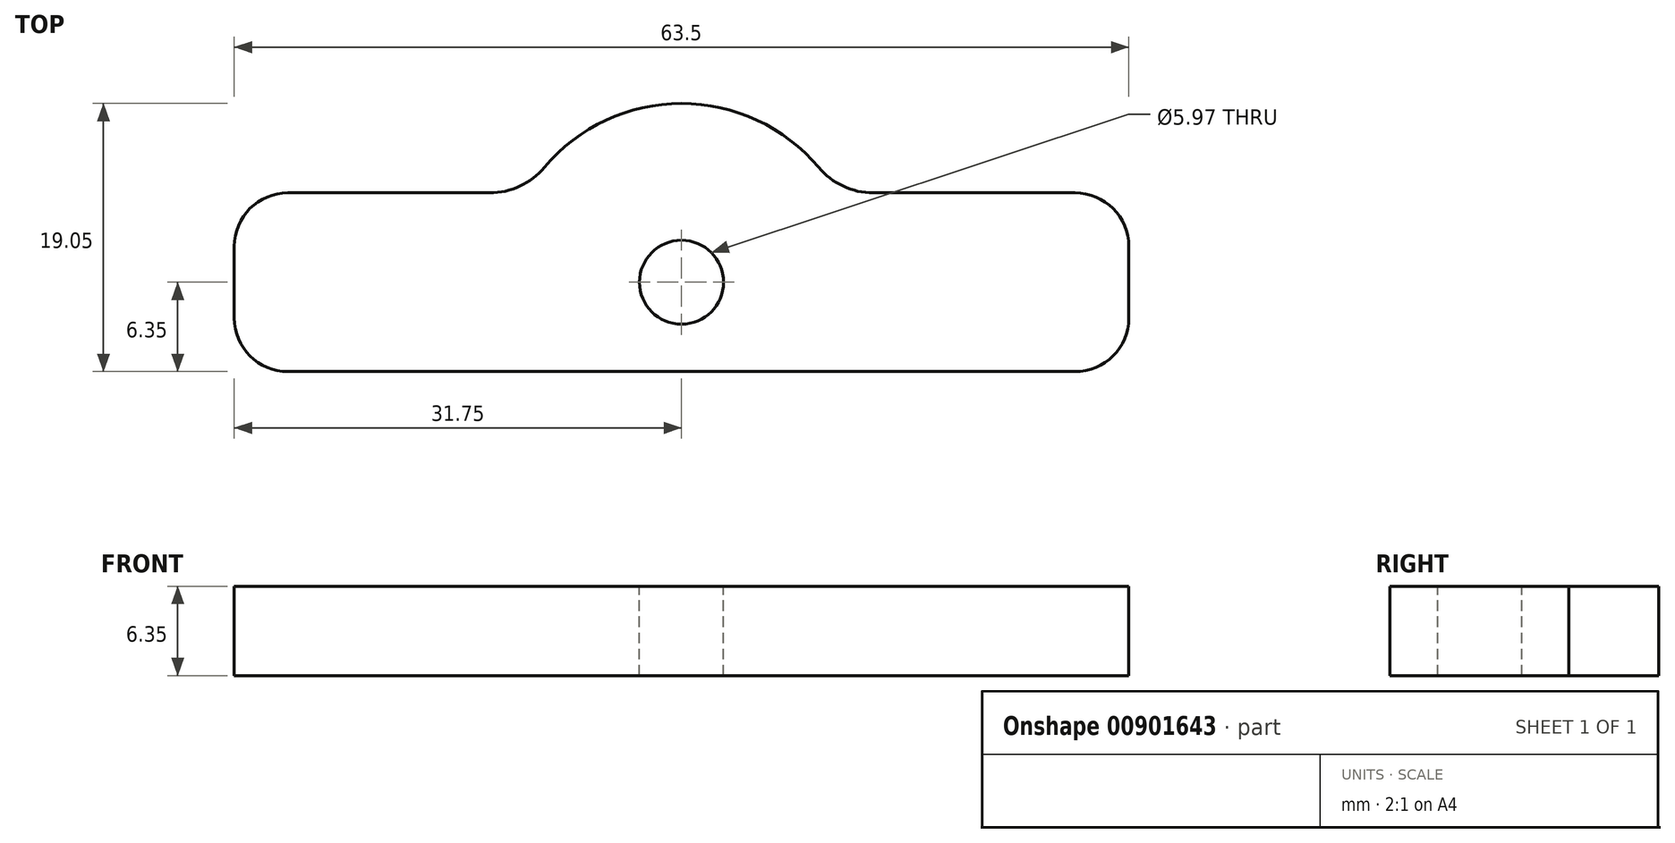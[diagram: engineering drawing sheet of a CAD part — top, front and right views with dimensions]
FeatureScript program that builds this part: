
annotation { "Feature Type Name" : "Feature", "Feature Type Description" : "" }
export const myFeature = defineFeature(function(context is Context, id is Id, definition is map)
    precondition{}
    {
        {
            var Q0;
            Q0=qCreatedBy(makeId("Top.planeOp"),FACE);
            var sketch = newSketch(context, id + "F0", { "sketchPlane" : qUnion([Q0])});
            skCircle(sketch, "E0", {"center": v(0, 0) * mm, "radius": 12.7 * mm});
            skLineSegment(sketch, "E1.bottom", {"start": v(31.75, 6.35) * mm, "end": v(-31.75, 6.35) * mm});
            skLineSegment(sketch, "E1.top", {"start": v(31.75, -6.35) * mm, "end": v(-31.75, -6.35) * mm});
            skLineSegment(sketch, "E1.left", {"start": v(31.75, 6.35) * mm, "end": v(31.75, -6.35) * mm});
            skLineSegment(sketch, "E1.right", {"start": v(-31.75, 6.35) * mm, "end": v(-31.75, -6.35) * mm});
            skSolve(sketch);
        }
        {
            var Q0;
            {var subQ0=sQuery(id+"F0.wireOp",EDGE,"E1.bottom");var subQ1=sQuery(id+"F0.wireOp",EDGE,"E0");var subQ2=makeQuery(id+"F0.imprint","INTERSECT",VERTEX,{"disambiguationData":[OD(0.0)],"derivedFrom":[subQ1,subQ0]});Q0=makeQuery(id+"F0.imprint","IMPRINT",FACE,{"disambiguationData":[TD([[makeQuery(id+"F0.imprint","IMPRINT",EDGE,{"disambiguationData":[TD([[subQ2,-1.0]])],"derivedFrom":subQ1}),1.0]])]});}
            var Q1;
            {var subQ5=sQuery(id+"F0.wireOp",EDGE,"E1.right");Q1=makeQuery(id+"F0.imprint","IMPRINT",FACE,{"disambiguationData":[TD([[makeQuery(id+"F0.imprint","IMPRINT",EDGE,{"derivedFrom":subQ5}),1.0]])]});}
            var Q2;
            {var subQ0=sQuery(id+"F0.wireOp",EDGE,"E1.bottom");var subQ1=sQuery(id+"F0.wireOp",EDGE,"E0");var subQ2=makeQuery(id+"F0.imprint","INTERSECT",VERTEX,{"disambiguationData":[OD(0.0)],"derivedFrom":[subQ1,subQ0]});Q2=makeQuery(id+"F0.imprint","IMPRINT",FACE,{"disambiguationData":[TD([[makeQuery(id+"F0.imprint","IMPRINT",EDGE,{"disambiguationData":[TD([[subQ2,1.0]])],"derivedFrom":subQ1}),1.0]])]});}
            var Q3;
            {var subQ5=sQuery(id+"F0.wireOp",EDGE,"E1.left");Q3=makeQuery(id+"F0.imprint","IMPRINT",FACE,{"disambiguationData":[TD([[makeQuery(id+"F0.imprint","IMPRINT",EDGE,{"derivedFrom":subQ5}),-1.0]])]});}
            var Q4;
            {var subQ0=sQuery(id+"F0.wireOp",EDGE,"E1.top");var subQ1=sQuery(id+"F0.wireOp",EDGE,"E0");var subQ2=makeQuery(id+"F0.imprint","INTERSECT",VERTEX,{"disambiguationData":[OD(0.0)],"derivedFrom":[subQ1,subQ0]});Q4=makeQuery(id+"F0.imprint","IMPRINT",FACE,{"disambiguationData":[TD([[makeQuery(id+"F0.imprint","IMPRINT",EDGE,{"disambiguationData":[TD([[subQ2,-1.0]])],"derivedFrom":subQ1}),1.0]])]});}
            extrude(context, id + "F1", {"entities" : qUnion([Q0, Q1, Q2, Q3, Q4]), "depth" : 6.35 * mm, "offsetDistance" : 25.4 * mm});
        }
        {
            var Q0;
            Q0=makeQuery(id+"F1.opExtrude","CAP_FACE",FACE,{"disambiguationData":[OSD([sQuery(id+"F0.wireOp",EDGE,"E0"),sQuery(id+"F0.wireOp",EDGE,"E1.bottom"),sQuery(id+"F0.wireOp",EDGE,"E1.top"),sQuery(id+"F0.wireOp",EDGE,"E1.left"),sQuery(id+"F0.wireOp",EDGE,"E1.right")])],"isStart":false});
            var sketch = newSketch(context, id + "F2", { "sketchPlane" : qUnion([Q0])});
            skCircle(sketch, "E2", {"center": v(0, 0) * mm, "radius": 2.98 * mm});
            skSolve(sketch);
        }
        {
            var Q0;
            Q0=makeQuery(id+"F2.imprint","IMPRINT",FACE,{"disambiguationData":[TD([[makeQuery(id+"F2.imprint","IMPRINT",EDGE,{"derivedFrom":sQuery(id+"F2.wireOp",EDGE,"E2")}),1.0]])]});
            extrude(context, id + "F3", {"entities" : qUnion([Q0]), "operationType" : NewBodyOperationType.REMOVE, "oppositeDirection" : true, "depth" : 6.35 * mm, "offsetDistance" : 25.4 * mm});
        }
        {
            var Q0;
            {var subQ0=sQuery(id+"F0.wireOp",EDGE,"E1.bottom");var subQ1=sQuery(id+"F0.wireOp",EDGE,"E0");Q0=makeQuery(id+"F1.opExtrude","SWEPT_EDGE",EDGE,{"disambiguationData":[OSD([subQ1,subQ0]),TDD([makeQuery(id+"F0.imprint","INTERSECT",VERTEX,{"disambiguationData":[OD(1.0)],"derivedFrom":[subQ1,subQ0]})])]});}
            var Q1;
            {var subQ0=sQuery(id+"F0.wireOp",EDGE,"E1.top");var subQ1=sQuery(id+"F0.wireOp",EDGE,"E0");Q1=makeQuery(id+"F1.opExtrude","SWEPT_EDGE",EDGE,{"disambiguationData":[OSD([subQ1,subQ0]),TDD([makeQuery(id+"F0.imprint","INTERSECT",VERTEX,{"disambiguationData":[OD(1.0)],"derivedFrom":[subQ1,subQ0]})])]});}
            var Q2;
            {var subQ0=sQuery(id+"F0.wireOp",EDGE,"E1.top");var subQ1=sQuery(id+"F0.wireOp",EDGE,"E0");Q2=makeQuery(id+"F1.opExtrude","SWEPT_EDGE",EDGE,{"disambiguationData":[OSD([subQ1,subQ0]),TDD([makeQuery(id+"F0.imprint","INTERSECT",VERTEX,{"disambiguationData":[OD(0.0)],"derivedFrom":[subQ1,subQ0]})])]});}
            var Q3;
            {var subQ0=sQuery(id+"F0.wireOp",EDGE,"E1.bottom");var subQ1=sQuery(id+"F0.wireOp",EDGE,"E0");Q3=makeQuery(id+"F1.opExtrude","SWEPT_EDGE",EDGE,{"disambiguationData":[OSD([subQ1,subQ0]),TDD([makeQuery(id+"F0.imprint","INTERSECT",VERTEX,{"disambiguationData":[OD(0.0)],"derivedFrom":[subQ1,subQ0]})])]});}
            fillet(context, id + "F4", {"entities" : qUnion([Q0, Q1, Q2, Q3]), "radius" : 5.08 * mm, "tangentPropagation" : true, "allowEdgeOverflow" : false});
        }
        {
            var Q0;
            Q0=makeQuery(id+"F1.opExtrude","SWEPT_EDGE",EDGE,{"disambiguationData":[OSD([sQuery(id+"F0.wireOp",EDGE,"E1.bottom"),sQuery(id+"F0.wireOp",EDGE,"E1.right")])]});
            var Q1;
            Q1=makeQuery(id+"F1.opExtrude","SWEPT_EDGE",EDGE,{"disambiguationData":[OSD([sQuery(id+"F0.wireOp",EDGE,"E1.top"),sQuery(id+"F0.wireOp",EDGE,"E1.right")])]});
            var Q2;
            Q2=makeQuery(id+"F1.opExtrude","SWEPT_EDGE",EDGE,{"disambiguationData":[OSD([sQuery(id+"F0.wireOp",EDGE,"E1.top"),sQuery(id+"F0.wireOp",EDGE,"E1.left")])]});
            var Q3;
            Q3=makeQuery(id+"F1.opExtrude","SWEPT_EDGE",EDGE,{"disambiguationData":[OSD([sQuery(id+"F0.wireOp",EDGE,"E1.bottom"),sQuery(id+"F0.wireOp",EDGE,"E1.left")])]});
            fillet(context, id + "F5", {"entities" : qUnion([Q0, Q1, Q2, Q3]), "radius" : 3.8 * mm, "tangentPropagation" : true, "allowEdgeOverflow" : false});
        }
    });
